# Revit family: Water_Heaters_HAJDU_HAJDU-HB-300-C1_
name_source: partatom
category: Mechanical Equipment
units: mm (PartAtom-declared; Revit-internal decimal feet)

## family parameters
Always vertical = Yes
Classification = None
Cut with Voids When Loaded = No
Maintain Annotation Orientation = No
OmniClass Number = 23.31.29.13
OmniClass Title = Hot Water Tank Heaters
Part Type = Normal
Room Calculation Point = No
Round Connector Dimension = Use Diameter
Shared = No
Work Plane-Based = Yes

## types (1)
- HB 300 C1
    COP 7 °C = 2.45
    Case Material = Hajdu - Felület - Fehér
    Cirkuláció bemenet = 19.05 mm  [stored 0.0625 ft]
    Csapolási profil = L
    Csatlakozás leírása = Elektromos csatlakozó
    Default Elevation = 1219.2 mm  [stored 4 ft]
    Description = A HAJDU hőszivattyús-forróvíztároló a tartályban lévő víz felmelegítéséhez szükséges energia 70%-át a levegőben korlátlan mennyiségben rendelkezésre álló energiából nyeri. Ezzel a környezetbarát technológiával a tárolóban lévő vizet max.60°C-ra melegíthetjük fel úgy, hogy 1kWh villamos-energia felhasználásával 3,7kWh hő-energiát állítunk elő. Az energiatakarékos és környezetbarát melegvíz készítéssel párhuzamosan a hőszivattyús forróvíztárolóhoz csatlakoztatott légtechnika lehetővé teszi egy lakás szellőztetését, páramentesítését, vagy akár a klimatizálását is. Fűtési időszakban célszerű az 500m3/óra tömegáramú hideg levegőt kivezetni az épületből. A HAJDU Hőszivattyú -7°C –os levegővel is képes üzemelni, de 0°C- alatt célszerű a hibrid üzemmódot választani, ahol egy 1800 W-os elektromos fűtőbetét segíti a melegvíz elkészítését. A tartály korrózió elleni védelmét tűzzománc bevonat biztosítja, melyet beépített magnézium aktív-anód egészít ki. Természetesen a készülékeink anódfogyás kijelzővel rendelkeznek, amely az anód állapotát, elhasználtságát mutatják. A HB200C, HB300C, HB300C1 típusú hőszivattyús forróvíztároló tartalmaz egy hőcserélőt is, amellyel közvetlenül szolár rendszerhez is csatlakoztatható, de akár egy helység fűtési energiáját is szolgáltathatja.
    Elektromos bekötés = fix
    Energiahatékonysági osztály = A
    Feszültség = 230 V
    Frekvencia = 50 Hz
    Fázisok száma = 1
    Hocserélo felulete = 0.7 m2
    Hocserélo futoközeg belépés = 19.05 mm  [stored 0.0625 ft]
    Hocserélo futoközeg kilépés = 19.05 mm  [stored 0.0625 ft]
    Hutoközeg/mennyiség = R134a / 1100 g
    Kompresszor teljesítmény felvétel max. = 1200 W
    Kompresszor teljesítmény felvétel átlagos = 850 W
    Kondenzátor = biztonsági hőcserélő
    Korrózióvédelem = speciális tűzzománc + Mg anód
    Látszólagos terhelés = 3680 VA
    Légcsatorna csatlakozás = 190 mm  [stored 0.62336 ft]
    Légáramlás = 138.9 L/s
    Magasság = 1950 mm  [stored 6.39764 ft]
    Manufacturer = HAJDU
    Max. vízhomérséklet = 60 °C
    Mg-anód karbantartás = anódfogyás kijelző
    Model = HAJDU HB 300 C1
    Muködési homérséklet tartomány = - 7– +43 °C
    Mélység = 720 mm  [stored 2.3622 ft]
    Névleges urtartalom = 300 l
    Névleges üzemi nyomás = 0.6 MPa
    Product Page URL = https://hajdurt.hu
    Pótfuto teljesítmény = 1800 W
    Rádiusz = 330.5 mm  [stored 1.08432 ft]
    Teljesítménytényezo = 1
    Típus = levegő (beltéri)
    Tömeg = 136.00 kg
    URL = https://hajdurt.hu
    Védettségi fokozat = IPX4
    Vízcsatlakozás = 19.05 mm  [stored 0.0625 ft]
    Áramfelvétel = 16 A
    Átméro = 661 mm  [stored 2.16864 ft]
    Érintésvédelmi osztály = I.

note: [stored X ft] marks values corroborated as IEEE doubles in the binary element streams (Revit-internal decimal feet)

## geometry (parser evidence)
native form markers: Sweep x6
no freeform markers — native parametric forms only
